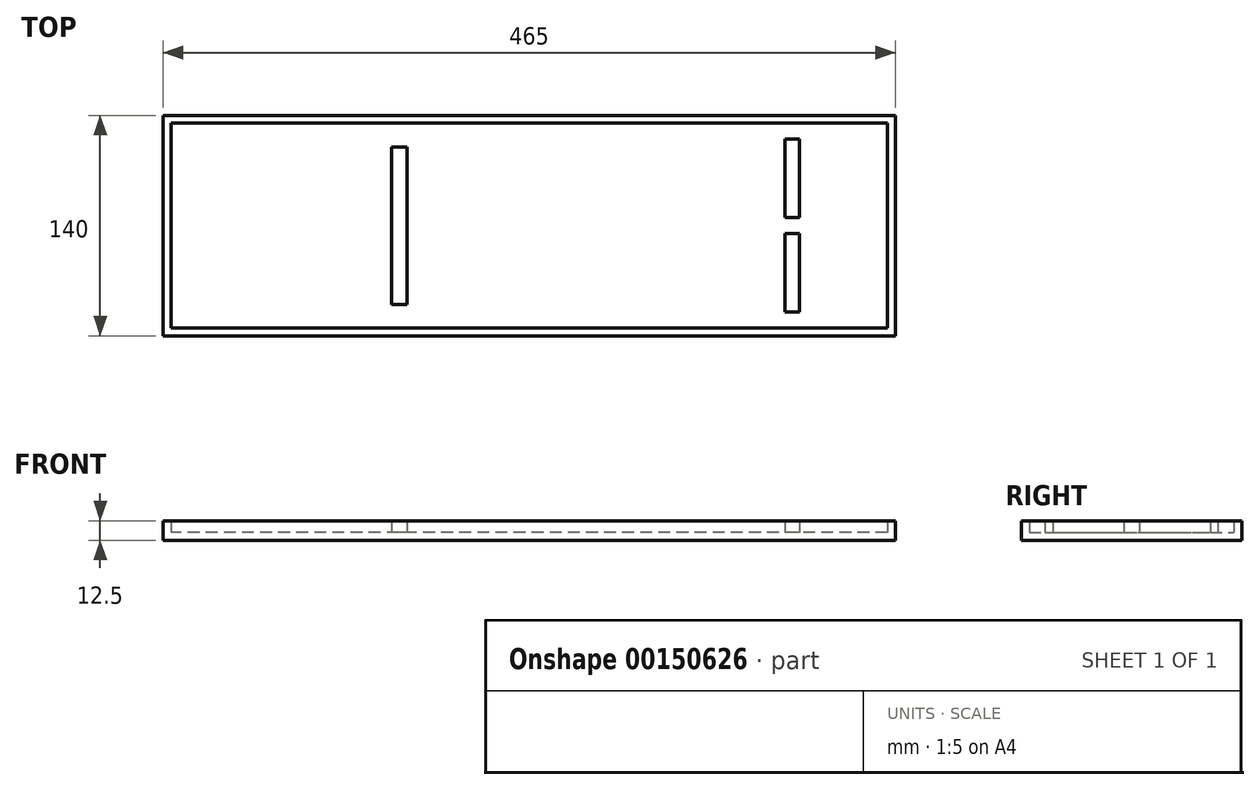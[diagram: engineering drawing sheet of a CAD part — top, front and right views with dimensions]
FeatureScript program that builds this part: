
annotation { "Feature Type Name" : "Feature", "Feature Type Description" : "" }
export const myFeature = defineFeature(function(context is Context, id is Id, definition is map)
    precondition{}
    {
        {
            var Q0;
            Q0=qCreatedBy(makeId("Top.planeOp"),FACE);
            var sketch = newSketch(context, id + "F0", { "sketchPlane" : qUnion([Q0])});
            skLineSegment(sketch, "E0.bottom", {"start": v(-206.46, 26.78) * mm, "end": v(258.54, 26.78) * mm});
            skLineSegment(sketch, "E0.top", {"start": v(-206.46, -113.22) * mm, "end": v(258.54, -113.22) * mm});
            skLineSegment(sketch, "E0.left", {"start": v(-206.46, 26.78) * mm, "end": v(-206.46, -113.22) * mm});
            skLineSegment(sketch, "E0.right", {"start": v(258.54, 26.78) * mm, "end": v(258.54, -113.22) * mm});
            skLineSegment(sketch, "E1.bottom", {"start": v(-201.46, 21.78) * mm, "end": v(253.54, 21.78) * mm});
            skLineSegment(sketch, "E1.top", {"start": v(-201.46, -108.22) * mm, "end": v(253.54, -108.22) * mm});
            skLineSegment(sketch, "E1.left", {"start": v(-201.46, 21.78) * mm, "end": v(-201.46, -108.22) * mm});
            skLineSegment(sketch, "E1.right", {"start": v(253.54, 21.78) * mm, "end": v(253.54, -108.22) * mm});
            skLineSegment(sketch, "E2", {"start": v(-201.46, 21.78) * mm, "end": v(-201.46, 26.78) * mm, "construction": true});
            skLineSegment(sketch, "E3", {"start": v(-201.46, 21.78) * mm, "end": v(-206.46, 21.78) * mm, "construction": true});
            skLineSegment(sketch, "E4", {"start": v(253.54, 21.78) * mm, "end": v(197.54, 21.78) * mm, "construction": true});
            skLineSegment(sketch, "E5", {"start": v(197.54, 21.78) * mm, "end": v(197.54, -108.22) * mm, "construction": true});
            skLineSegment(sketch, "E6", {"start": v(197.54, 21.78) * mm, "end": v(192.54, 21.78) * mm, "construction": true});
            skLineSegment(sketch, "E7", {"start": v(192.54, 21.78) * mm, "end": v(188.54, 21.78) * mm, "construction": true});
            skLineSegment(sketch, "E8", {"start": v(188.54, 21.78) * mm, "end": v(188.54, -108.22) * mm, "construction": true});
            skLineSegment(sketch, "E9", {"start": v(188.54, -108.22) * mm, "end": v(188.54, -98.22) * mm, "construction": true});
            skLineSegment(sketch, "E10", {"start": v(188.54, -98.22) * mm, "end": v(188.54, -48.22) * mm, "construction": true});
            skLineSegment(sketch, "E11", {"start": v(188.54, -48.22) * mm, "end": v(188.54, -38.22) * mm, "construction": true});
            skLineSegment(sketch, "E12", {"start": v(188.54, -38.22) * mm, "end": v(188.54, 11.78) * mm, "construction": true});
            skLineSegment(sketch, "E13.bottom", {"start": v(188.54, 11.78) * mm, "end": v(197.54, 11.78) * mm});
            skLineSegment(sketch, "E13.top", {"start": v(188.54, -38.22) * mm, "end": v(197.54, -38.22) * mm});
            skLineSegment(sketch, "E13.left", {"start": v(188.54, 11.78) * mm, "end": v(188.54, -38.22) * mm});
            skLineSegment(sketch, "E13.right", {"start": v(197.54, 11.78) * mm, "end": v(197.54, -38.22) * mm});
            skLineSegment(sketch, "E14.bottom", {"start": v(188.54, -48.22) * mm, "end": v(197.54, -48.22) * mm});
            skLineSegment(sketch, "E14.top", {"start": v(188.54, -98.22) * mm, "end": v(197.54, -98.22) * mm});
            skLineSegment(sketch, "E14.left", {"start": v(188.54, -48.22) * mm, "end": v(188.54, -98.22) * mm});
            skLineSegment(sketch, "E14.right", {"start": v(197.54, -48.22) * mm, "end": v(197.54, -98.22) * mm});
            skLineSegment(sketch, "E15", {"start": v(-206.46, 26.78) * mm, "end": v(-56.46, 26.78) * mm, "construction": true});
            skLineSegment(sketch, "E16", {"start": v(-56.46, 26.78) * mm, "end": v(-56.46, -108.22) * mm, "construction": true});
            skLineSegment(sketch, "E17", {"start": v(-56.46, 26.78) * mm, "end": v(-61.46, 26.78) * mm, "construction": true});
            skLineSegment(sketch, "E18", {"start": v(-61.46, 26.78) * mm, "end": v(-61.46, -108.22) * mm, "construction": true});
            skLineSegment(sketch, "E19", {"start": v(-56.46, 26.78) * mm, "end": v(-51.46, 26.78) * mm, "construction": true});
            skLineSegment(sketch, "E20", {"start": v(-51.46, 26.78) * mm, "end": v(-51.46, -108.22) * mm, "construction": true});
            skLineSegment(sketch, "E21", {"start": v(-61.46, -108.22) * mm, "end": v(-61.46, -93.22) * mm, "construction": true});
            skLineSegment(sketch, "E22", {"start": v(-61.46, -93.22) * mm, "end": v(-61.46, 6.78) * mm, "construction": true});
            skLineSegment(sketch, "E23.bottom", {"start": v(-61.46, 6.78) * mm, "end": v(-51.46, 6.78) * mm});
            skLineSegment(sketch, "E23.top", {"start": v(-61.46, -93.22) * mm, "end": v(-51.46, -93.22) * mm});
            skLineSegment(sketch, "E23.left", {"start": v(-61.46, 6.78) * mm, "end": v(-61.46, -93.22) * mm});
            skLineSegment(sketch, "E23.right", {"start": v(-51.46, 6.78) * mm, "end": v(-51.46, -93.22) * mm});
            skCircle(sketch, "E24", {"center": v(-191.46, -98.22) * mm, "radius": 7.5 * mm, "construction": true});
            skCircle(sketch, "E25", {"center": v(-191.46, 11.78) * mm, "radius": 7.5 * mm, "construction": true});
            skSolve(sketch);
        }
        {
            var Q0;
            Q0=makeQuery(id+"F0.imprint","IMPRINT",FACE,{"disambiguationData":[TD([[makeQuery(id+"F0.imprint","IMPRINT",EDGE,{"derivedFrom":sQuery(id+"F0.wireOp",EDGE,"E1.bottom")}),-1.0]])]});
            var Q1;
            Q1=makeQuery(id+"F0.imprint","IMPRINT",FACE,{"disambiguationData":[TD([[makeQuery(id+"F0.imprint","IMPRINT",EDGE,{"derivedFrom":sQuery(id+"F0.wireOp",EDGE,"E0.bottom")}),-1.0]])]});
            var Q2;
            Q2=makeQuery(id+"F0.imprint","IMPRINT",FACE,{"disambiguationData":[TD([[makeQuery(id+"F0.imprint","IMPRINT",EDGE,{"derivedFrom":sQuery(id+"F0.wireOp",EDGE,"E23.bottom")}),-1.0]])]});
            var Q3;
            Q3=makeQuery(id+"F0.imprint","IMPRINT",FACE,{"disambiguationData":[TD([[makeQuery(id+"F0.imprint","IMPRINT",EDGE,{"derivedFrom":sQuery(id+"F0.wireOp",EDGE,"E13.bottom")}),-1.0]])]});
            var Q4;
            Q4=makeQuery(id+"F0.imprint","IMPRINT",FACE,{"disambiguationData":[TD([[makeQuery(id+"F0.imprint","IMPRINT",EDGE,{"derivedFrom":sQuery(id+"F0.wireOp",EDGE,"E14.bottom")}),-1.0]])]});
            extrude(context, id + "F1", {"entities" : qUnion([Q0, Q1, Q2, Q3, Q4]), "depth" : 5 * mm});
        }
        {
            var Q0;
            Q0=makeQuery(id+"F0.imprint","IMPRINT",FACE,{"disambiguationData":[TD([[makeQuery(id+"F0.imprint","IMPRINT",EDGE,{"derivedFrom":sQuery(id+"F0.wireOp",EDGE,"E0.bottom")}),-1.0]])]});
            var Q1;
            Q1=makeQuery(id+"F0.imprint","IMPRINT",FACE,{"disambiguationData":[TD([[makeQuery(id+"F0.imprint","IMPRINT",EDGE,{"derivedFrom":sQuery(id+"F0.wireOp",EDGE,"E23.bottom")}),-1.0]])]});
            var Q2;
            Q2=makeQuery(id+"F0.imprint","IMPRINT",FACE,{"disambiguationData":[TD([[makeQuery(id+"F0.imprint","IMPRINT",EDGE,{"derivedFrom":sQuery(id+"F0.wireOp",EDGE,"E13.bottom")}),-1.0]])]});
            var Q3;
            Q3=makeQuery(id+"F0.imprint","IMPRINT",FACE,{"disambiguationData":[TD([[makeQuery(id+"F0.imprint","IMPRINT",EDGE,{"derivedFrom":sQuery(id+"F0.wireOp",EDGE,"E14.bottom")}),-1.0]])]});
            extrude(context, id + "F2", {"entities" : qUnion([Q0, Q1, Q2, Q3]), "operationType" : NewBodyOperationType.ADD, "depth" : 12.5 * mm});
        }
    });
